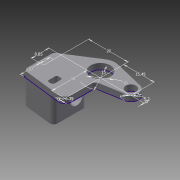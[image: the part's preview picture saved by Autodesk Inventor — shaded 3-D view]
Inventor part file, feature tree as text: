
AUTODESK INVENTOR PART (.ipt)
format: ipt  version: 2015 (Build 190159000, 159)  size: 206,336 bytes
history: native  units: mm
features: fillet x10, extrude x5, sketch x4, projected_geometry x2
ambient origin geometry x8: Origin, YZ Plane, XZ Plane, XY Plane, X Axis, Y Axis, Z Axis, Center Point
bodies: Body1 (feature_tree)
feature tree (21):
  sketch  "Sketch1"  dims[d0=15.45mm d1=5.2mm d2=10.0mm]
  extrude  "Extrusion3"  Depth=10.0mm
  fillet  "Fillet7"  Radius=10.0mm
  extrude  "Extrusion6"  Depth=7.7mm
  sketch  "Sketch5"  dims[d3=0.0mm d4=7.7mm]
  extrude  "Extrusion8"  Depth=2.0mm
  fillet  "Fillet8"  [1 undecoded]
  fillet  "Fillet9"  Radius=18.0mm
  fillet  "Fillet10"  Radius=8.85mm
  fillet  "Fillet11"  Radius=20.0mm
  fillet  "Fillet12"  Radius=5.0mm
  fillet  "Fillet13"  Radius=10.0mm
  fillet  "Fillet14"  Radius=3.0mm
  fillet  "Fillet18"  Radius=2.0mm
  extrude  "Extrusion9"  Depth=2.0mm
  extrude  "Extrusion10"  TaperAngle=0.0deg  [1 undecoded]
  fillet  "Fillet19"  Radius=6.15mm
  sketch  "Sketch6"  dims[d5=15.0mm d6=6.35mm d7=0.0mm d9=18.0mm d21=8.85mm d22=20.0mm d23=5.0mm d24=10.0mm d25=3.0mm d26=0.0mm d40=2.0mm]
  projected_geometry  "Projected Loop1"
  sketch  "Sketch8"  dims[d41=12.3mm d42=0.0mm d43=6.3mm d44=0.0mm d45=6.15mm d51=12.3mm d52=0.0mm d53=2.0mm d54=2.0mm d55=5.0mm d56=3.0mm d57=3.0mm d58=1.0mm d59=1.0mm d60=1.0mm d61=1.0mm d62=1.0mm d63=2.0mm d67=2.0mm d68=0.0mm d69=0.0mm d70=12.3mm d71=0.0mm d72=2.0mm]
  projected_geometry  "Projected Loop2"
note: 2 required parameter values undecoded (feature->parameter linkage not recoverable at this tier; creation-order binding heuristic only, values carry confidence <= 0.55)
